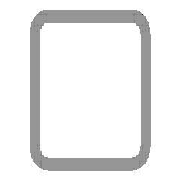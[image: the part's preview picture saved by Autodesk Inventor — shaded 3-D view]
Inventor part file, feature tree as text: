
AUTODESK INVENTOR PART (.ipt)
format: ipt  version: 2025 (Build 290162010, 162A)  size: 134,656 bytes
history: native  units: mm (DEFAULTED — no unit token found)
features: other x4, sketch x1, plane x1
ambient origin geometry x8: Origin, YZ Plane, XZ Plane, XY Plane, X Axis, Y Axis, Z Axis, Center Point
bodies: Solid1 (feature_tree), Body (feature_tree)
feature tree (6):
  parser-record x1  (decoder bookkeeping rows leaked as tree rows — omitted from the tree; the rows remain in map.json)
  other  "Driven Length"
  other  "Start Plane"
  other  "End Plane"
  sketch  "Sketch3"  dims[d3=2209.072203mm d4=0.0mm d7=6.0mm d9=100.0mm d11=100.0mm d12=3.0mm d13=-0.0mm d14=2209.072203mm d15=50.0mm d16=50.0mm d17=90.0deg d18=2209.072203mm]
  plane  "Work Plane3"
